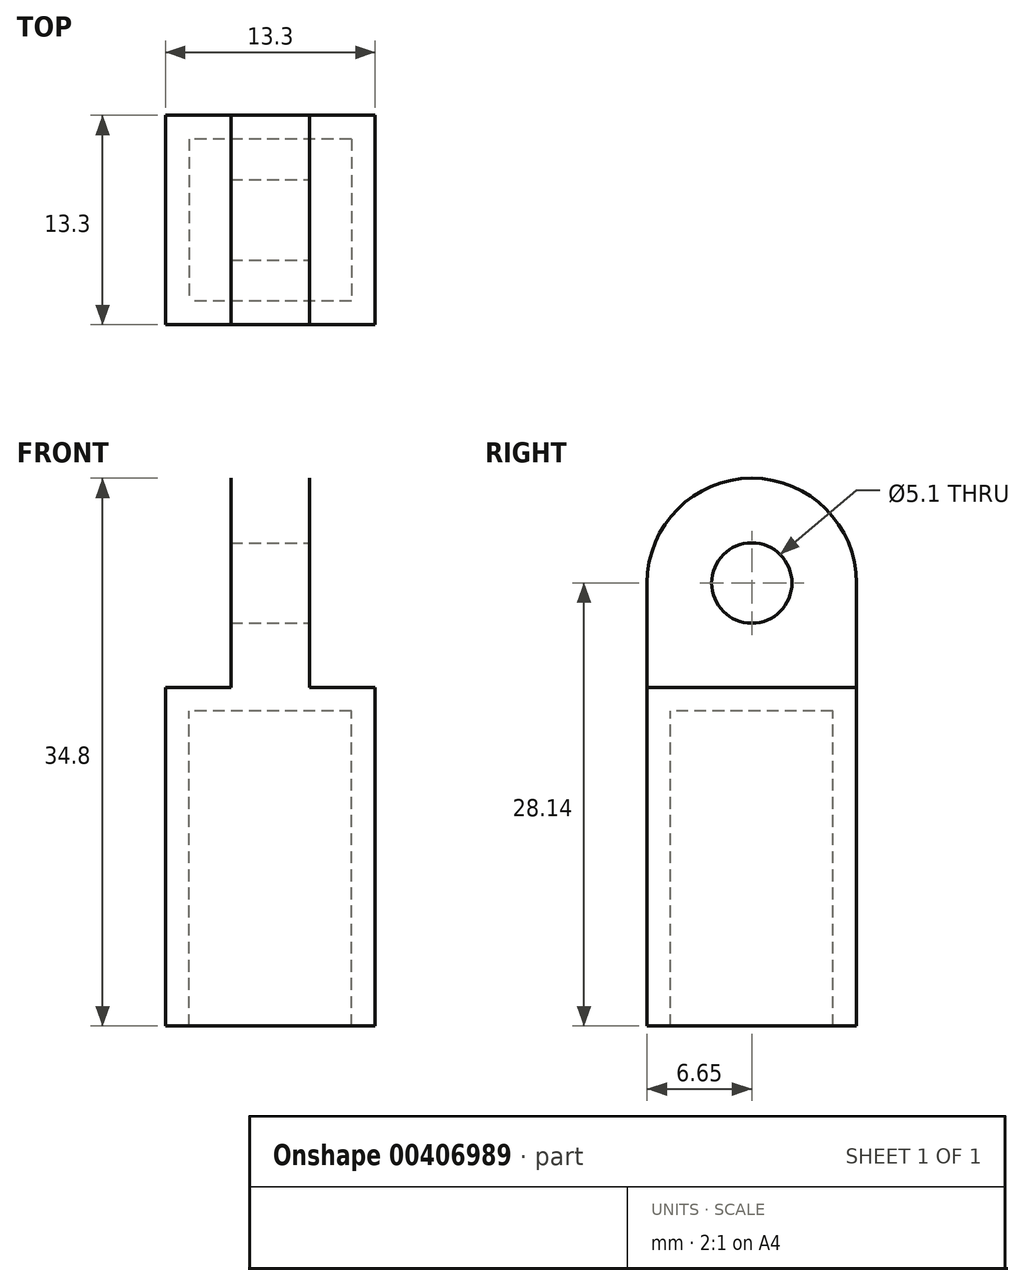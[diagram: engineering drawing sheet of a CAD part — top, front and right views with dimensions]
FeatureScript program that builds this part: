
annotation { "Feature Type Name" : "Feature", "Feature Type Description" : "" }
export const myFeature = defineFeature(function(context is Context, id is Id, definition is map)
    precondition{}
    {
        {
            var Q0;
            Q0=qCreatedBy(makeId("Top.planeOp"),FACE);
            var sketch = newSketch(context, id + "F0", { "sketchPlane" : qUnion([Q0])});
            skLineSegment(sketch, "E0.bottom", {"start": v(5.15, 5.15) * mm, "end": v(-5.15, 5.15) * mm});
            skLineSegment(sketch, "E0.top", {"start": v(5.15, -5.15) * mm, "end": v(-5.15, -5.15) * mm});
            skLineSegment(sketch, "E0.left", {"start": v(5.15, 5.15) * mm, "end": v(5.15, -5.15) * mm});
            skLineSegment(sketch, "E0.right", {"start": v(-5.15, 5.15) * mm, "end": v(-5.15, -5.15) * mm});
            skPoint(sketch, "E0.middle", {"position": v(0, 0) * mm});
            skLineSegment(sketch, "E1.bottom", {"start": v(6.65, 6.65) * mm, "end": v(-6.65, 6.65) * mm});
            skLineSegment(sketch, "E1.top", {"start": v(6.65, -6.65) * mm, "end": v(-6.65, -6.65) * mm});
            skLineSegment(sketch, "E1.left", {"start": v(6.65, 6.65) * mm, "end": v(6.65, -6.65) * mm});
            skLineSegment(sketch, "E1.right", {"start": v(-6.65, 6.65) * mm, "end": v(-6.65, -6.65) * mm});
            skSolve(sketch);
        }
        {
            var Q0;
            Q0=makeQuery(id+"F0.imprint","IMPRINT",FACE,{"disambiguationData":[TD([[makeQuery(id+"F0.imprint","IMPRINT",EDGE,{"derivedFrom":sQuery(id+"F0.wireOp",EDGE,"E0.bottom")}),-1.0]])]});
            extrude(context, id + "F1", {"entities" : qUnion([Q0]), "oppositeDirection" : true, "depth" : 20 * mm});
        }
        {
            var Q0;
            Q0=makeQuery(id+"F0.imprint","IMPRINT",FACE,{"disambiguationData":[TD([[makeQuery(id+"F0.imprint","IMPRINT",EDGE,{"derivedFrom":sQuery(id+"F0.wireOp",EDGE,"E0.bottom")}),1.0]])]});
            var Q1;
            Q1=makeQuery(id+"F0.imprint","IMPRINT",FACE,{"disambiguationData":[TD([[makeQuery(id+"F0.imprint","IMPRINT",EDGE,{"derivedFrom":sQuery(id+"F0.wireOp",EDGE,"E0.bottom")}),-1.0]])]});
            extrude(context, id + "F2", {"entities" : qUnion([Q0, Q1]), "operationType" : NewBodyOperationType.ADD, "depth" : 1.5 * mm});
        }
        {
            var Q0;
            Q0=makeQuery(id+"F2.opExtrude","CAP_FACE",FACE,{"disambiguationData":[OSD([sQuery(id+"F0.wireOp",EDGE,"E1.bottom"),sQuery(id+"F0.wireOp",EDGE,"E1.top"),sQuery(id+"F0.wireOp",EDGE,"E1.left"),sQuery(id+"F0.wireOp",EDGE,"E1.right")])],"isStart":false});
            var sketch = newSketch(context, id + "F3", { "sketchPlane" : qUnion([Q0])});
            skLineSegment(sketch, "E2.bottom", {"start": v(2.5, 6.65) * mm, "end": v(-2.5, 6.65) * mm});
            skLineSegment(sketch, "E2.top", {"start": v(2.5, -6.65) * mm, "end": v(-2.5, -6.65) * mm});
            skLineSegment(sketch, "E2.left", {"start": v(2.5, 6.65) * mm, "end": v(2.5, -6.65) * mm});
            skLineSegment(sketch, "E2.right", {"start": v(-2.5, 6.65) * mm, "end": v(-2.5, -6.65) * mm});
            skPoint(sketch, "E2.middle", {"position": v(0, 0) * mm});
            skSolve(sketch);
        }
        {
            var Q0;
            Q0=makeQuery(id+"F3.imprint","IMPRINT",FACE,{"disambiguationData":[TD([[makeQuery(id+"F3.imprint","IMPRINT",EDGE,{"derivedFrom":sQuery(id+"F3.wireOp",EDGE,"E2.bottom")}),1.0]])]});
            extrude(context, id + "F4", {"entities" : qUnion([Q0]), "operationType" : NewBodyOperationType.ADD, "depth" : 13.3 * mm});
        }
        {
            var Q0;
            Q0=makeQuery(id+"F4.opExtrude","CAP_EDGE",EDGE,{"disambiguationData":[OSD([sQuery(id+"F3.wireOp",EDGE,"E2.top")])],"isStart":false});
            var Q1;
            Q1=makeQuery(id+"F4.opExtrude","CAP_EDGE",EDGE,{"disambiguationData":[OSD([sQuery(id+"F3.wireOp",EDGE,"E2.bottom")])],"isStart":false});
            fillet(context, id + "F5", {"entities" : qUnion([Q0, Q1]), "radius" : 6.66 * mm, "tangentPropagation" : true, "allowEdgeOverflow" : false});
        }
        {
            var Q0;
            Q0=makeQuery(id+"F4.opExtrude","SWEPT_FACE",FACE,{"disambiguationData":[OSD([sQuery(id+"F3.wireOp",EDGE,"E2.left")])]});
            var sketch = newSketch(context, id + "F6", { "sketchPlane" : qUnion([Q0])});
            skCircle(sketch, "E3", {"center": v(0, 8.14) * mm, "radius": 2.55 * mm});
            skSolve(sketch);
        }
        {
            var Q0;
            Q0=makeQuery(id+"F6.imprint","IMPRINT",FACE,{"disambiguationData":[TD([[makeQuery(id+"F6.imprint","IMPRINT",EDGE,{"derivedFrom":sQuery(id+"F6.wireOp",EDGE,"E3")}),1.0]])]});
            extrude(context, id + "F7", {"entities" : qUnion([Q0]), "operationType" : NewBodyOperationType.REMOVE, "oppositeDirection" : true, "depth" : 25 * mm, "hasSecondDirection" : true, "secondDirectionOppositeDirection" : false, "secondDirectionDepth" : 25 * mm});
        }
    });
